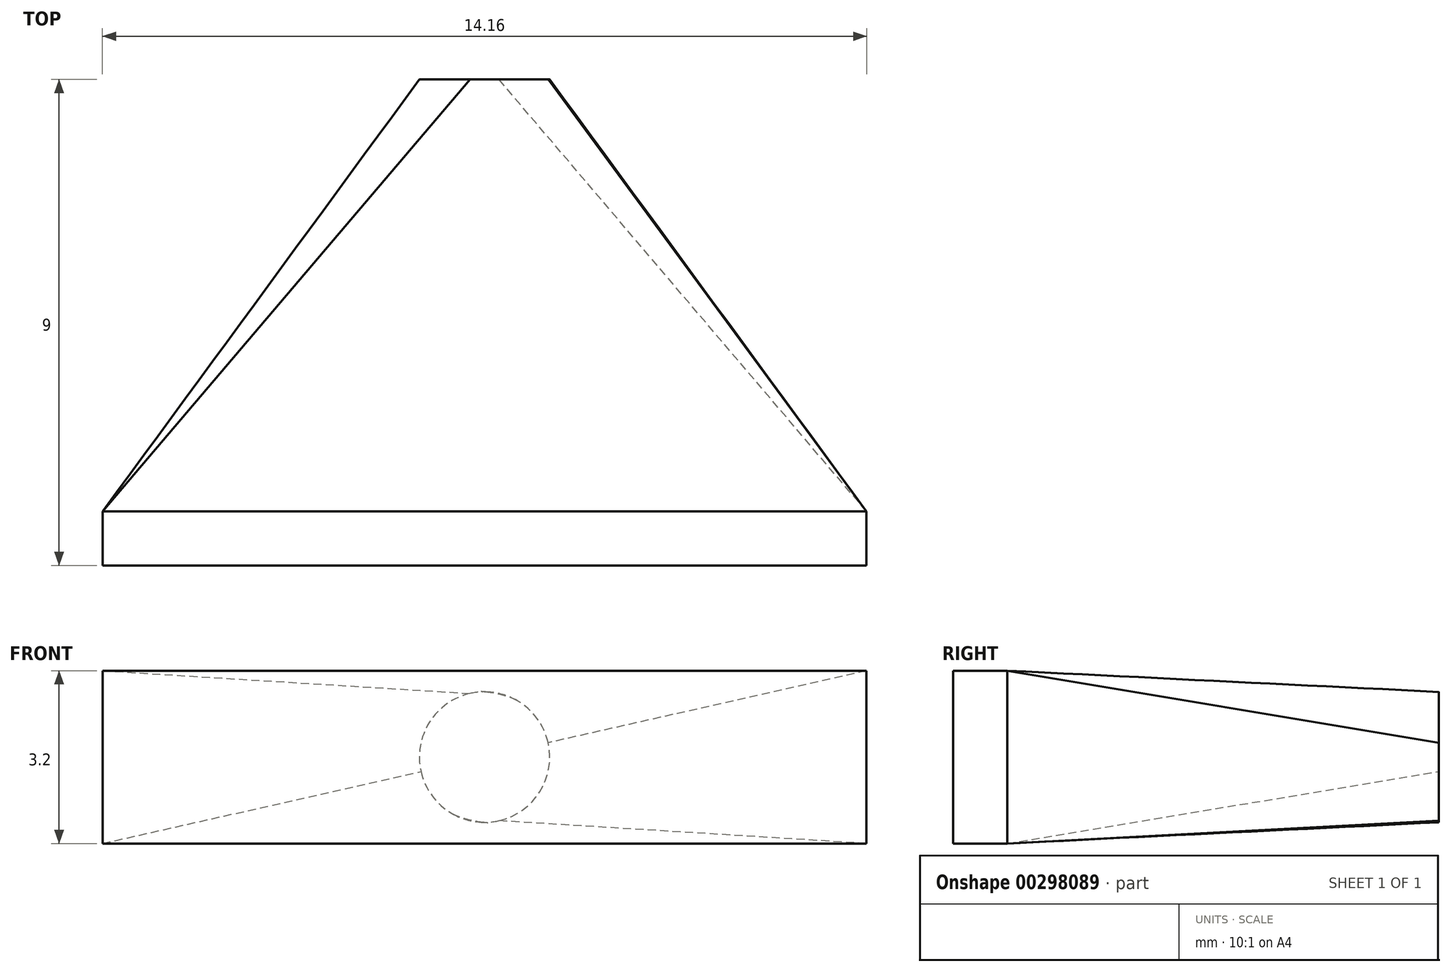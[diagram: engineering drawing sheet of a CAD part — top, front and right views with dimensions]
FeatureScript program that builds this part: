
annotation { "Feature Type Name" : "Feature", "Feature Type Description" : "" }
export const myFeature = defineFeature(function(context is Context, id is Id, definition is map)
    precondition{}
    {
        {
            var Q0;
            Q0=qCreatedBy(makeId("Front.planeOp"),FACE);
            var sketch = newSketch(context, id + "F0", { "sketchPlane" : qUnion([Q0])});
            skCircle(sketch, "E0", {"center": v(0, 0) * mm, "radius": 1.2 * mm});
            skSolve(sketch);
        }
        {
            var Q0;
            Q0=qCreatedBy(makeId("Front.planeOp"),FACE);
            cPlane(context, id + "F1", {"entities" : qUnion([Q0]), "cplaneType" : CPlaneType.OFFSET, "offset" : 8 * mm, "width" : 150 * mm, "height" : 150 * mm});
        }
        {
            var Q0;
            Q0=qCreatedBy(id+"F1.planeOp",FACE);
            var sketch = newSketch(context, id + "F2", { "sketchPlane" : qUnion([Q0])});
            skLineSegment(sketch, "E1.bottom", {"start": v(7.08, 1.6) * mm, "end": v(-7.08, 1.6) * mm});
            skLineSegment(sketch, "E1.top", {"start": v(7.08, -1.6) * mm, "end": v(-7.08, -1.6) * mm});
            skLineSegment(sketch, "E1.left", {"start": v(7.08, 1.6) * mm, "end": v(7.08, -1.6) * mm});
            skLineSegment(sketch, "E1.right", {"start": v(-7.08, 1.6) * mm, "end": v(-7.08, -1.6) * mm});
            skPoint(sketch, "E1.middle", {"position": v(0, 0) * mm});
            skSolve(sketch);
        }
        {
            var Q0;
            Q0=makeQuery(id+"F2.imprint","IMPRINT",FACE,{"disambiguationData":[TD([[makeQuery(id+"F2.imprint","IMPRINT",EDGE,{"derivedFrom":sQuery(id+"F2.wireOp",EDGE,"E1.bottom")}),1.0]])]});
            var Q1;
            Q1=makeQuery(id+"F0.imprint","IMPRINT",FACE,{"disambiguationData":[TD([[makeQuery(id+"F0.imprint","IMPRINT",EDGE,{"derivedFrom":sQuery(id+"F0.wireOp",EDGE,"E0")}),1.0]])]});
            loft(context, id + "F3", {"sheetProfilesArray" : [{ "sheetProfileEntities" : qUnion([Q0]) }, { "sheetProfileEntities" : qUnion([Q1]) }]});
        }
        {
            var Q0;
            Q0=makeQuery(id+"F3.opLoft","CAP_FACE",FACE,{"disambiguationData":[OSD([makeQuery(id+"F2.imprint","IMPRINT",FACE,{"disambiguationData":[TD([[makeQuery(id+"F2.imprint","IMPRINT",EDGE,{"derivedFrom":sQuery(id+"F2.wireOp",EDGE,"E1.bottom")}),1.0]])]})])],"isStart":true});
            var sketch = newSketch(context, id + "F4", { "sketchPlane" : qUnion([Q0])});
            skLineSegment(sketch, "E2.0.0", {"start": v(-7.08, -1.6) * mm, "end": v(7.08, -1.6) * mm});
            skLineSegment(sketch, "E2.0.1", {"start": v(7.08, -1.6) * mm, "end": v(7.08, 1.6) * mm});
            skLineSegment(sketch, "E2.0.2", {"start": v(-7.08, 1.6) * mm, "end": v(7.08, 1.6) * mm});
            skLineSegment(sketch, "E2.0.3", {"start": v(-7.08, -1.6) * mm, "end": v(-7.08, 1.6) * mm});
            skSolve(sketch);
        }
        {
            var Q0;
            Q0=makeQuery(id+"F4.imprint","IMPRINT",FACE,{"disambiguationData":[TD([[makeQuery(id+"F4.imprint","IMPRINT",EDGE,{"derivedFrom":sQuery(id+"F4.wireOp",EDGE,"E2.0.0")}),-1.0]])]});
            extrude(context, id + "F5", {"entities" : qUnion([Q0]), "operationType" : NewBodyOperationType.ADD, "depth" : 1 * mm});
        }
    });
